# Revit family: Seating-Casual-Naughtone-Cloud_Plain_Three_Seat
name_source: partatom
category: Furniture
revit_build: Autodesk Revit 2014 (Build: 20140709_2115(x64)
units: mm (PartAtom-declared; Revit-internal decimal feet)

## types (2) — shared parameters
Additional Material = Additional material and finish options available. Please contact Naughtone direct for further information.
COBie Description = Designed by Naughtone, Cloud plain seating system's tactile, pillowy surround is designed to invite and comfort without consuming masses of space. Whether you are looking for somewhere to shelter or meet or simply to relax, cloud has a magnetic appeal.
Current Revision = 1
Depth = 750 mm  [stored 2.46063 ft]
Length = 2100 mm  [stored 6.88976 ft]
Manufacturer = Naughtone
Name = Furniture-Seating-Casual-Cloud_Plain
Product URL = http://www.naughtone.com
URL = http://www.naughtone.com
Uniclass = Pr_40_50_12_81
WarrantyDuration = 60
zero-valued in all types: Barcode, Cost, SerialNumber, TagNumber

## per-type parameters (varying)
| type | Description | Height | High Chair | Low Chair | Model | TypeName |
| CLO-P-3-HI | Cloud Three Seat Sofa with High Back | 1300 mm  [stored 4.26509 ft] | Yes | No | Cloud Three Seat Sofa with High Back | 2100mmx750mm1300mm, Cloud Plain |
| CLO-P-3-LO | Cloud Three Seat Sofa with Low Back | 650 mm | No | Yes | Cloud Three Seat Sofa with Low Back | 2100mmx750mm650mm, Cloud Plain Seating |

note: column(s) folded — value = type name in every type: AssetIdentifier, Product Code

note: [stored X ft] marks values corroborated as IEEE doubles in the binary element streams (Revit-internal decimal feet)

## geometry (parser evidence)
native form markers: Blend x2, Sweep x5
no freeform markers — native parametric forms only
